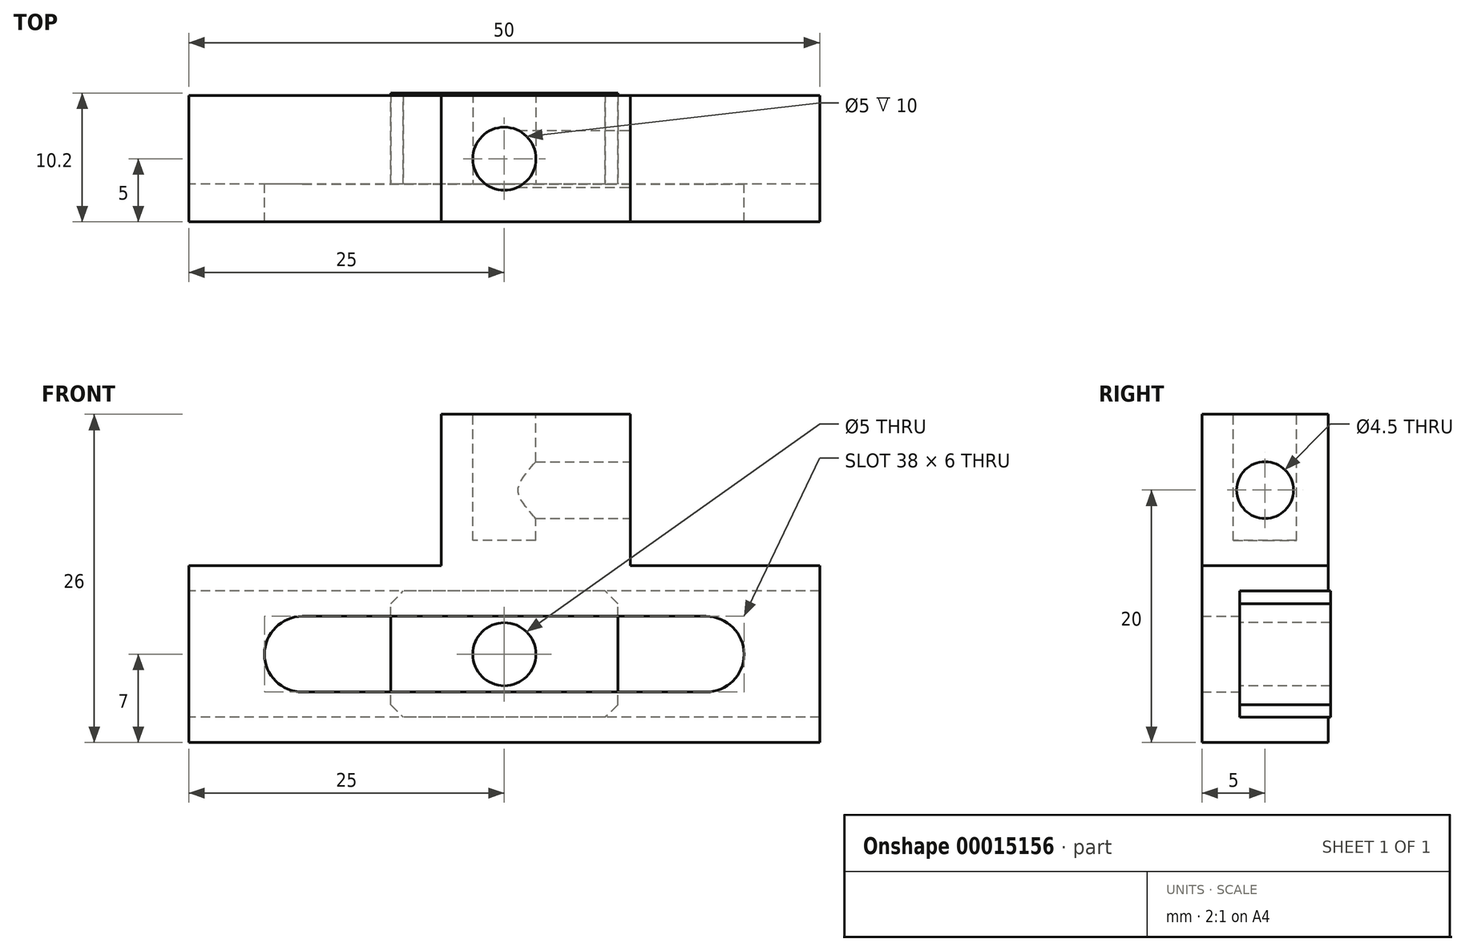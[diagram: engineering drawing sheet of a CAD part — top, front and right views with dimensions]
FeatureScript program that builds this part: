
annotation { "Feature Type Name" : "Feature", "Feature Type Description" : "" }
export const myFeature = defineFeature(function(context is Context, id is Id, definition is map)
    precondition{}
    {
        {
            var Q0;
            Q0=qCreatedBy(makeId("Right.planeOp"),FACE);
            var sketch = newSketch(context, id + "F0", { "sketchPlane" : qUnion([Q0])});
            skLineSegment(sketch, "E0.rect.bottom", {"start": v(5, -7) * mm, "end": v(-5, -7) * mm});
            skLineSegment(sketch, "E0.rect.top", {"start": v(5, 7) * mm, "end": v(-5, 7) * mm});
            skLineSegment(sketch, "E0.rect.left", {"start": v(5, -7) * mm, "end": v(5, -5) * mm});
            skLineSegment(sketch, "E0.rect.right", {"start": v(-5, -7) * mm, "end": v(-5, 7) * mm});
            skPoint(sketch, "E0.rect.middle", {"position": v(0, 0) * mm});
            skLineSegment(sketch, "E1", {"start": v(5, 5) * mm, "end": v(-2, 5) * mm});
            skLineSegment(sketch, "E2", {"start": v(-2, 5) * mm, "end": v(-2, -5) * mm});
            skLineSegment(sketch, "E3", {"start": v(-2, -5) * mm, "end": v(5, -5) * mm});
            skLineSegment(sketch, "E4", {"start": v(7.33, 0) * mm, "end": v(-10.47, 0) * mm, "construction": true});
            skLineSegment(sketch, "E5.trimOffspring", {"start": v(5, 5) * mm, "end": v(5, 7) * mm});
            skSolve(sketch);
        }
        {
            var Q0;
            Q0=makeQuery(id+"F0.imprint","IMPRINT",FACE,{"disambiguationData":[TD([[makeQuery(id+"F0.imprint","IMPRINT",EDGE,{"derivedFrom":sQuery(id+"F0.wireOp",EDGE,"E0.rect.bottom")}),-1.0]])]});
            extrude(context, id + "F1", {"entities" : qUnion([Q0]), "endBound" : BoundingType.SYMMETRIC, "depth" : 50 * mm});
        }
        {
            var Q0;
            Q0=makeQuery(id+"F1.opExtrude","SWEPT_FACE",FACE,{"disambiguationData":[OSD([sQuery(id+"F0.wireOp",EDGE,"E2")])]});
            var sketch = newSketch(context, id + "F2", { "sketchPlane" : qUnion([Q0])});
            skLineSegment(sketch, "E6", {"start": v(25, 0) * mm, "end": v(-25, 0) * mm, "construction": true});
            skPoint(sketch, "E7", {"position": v(-16, 0) * mm});
            skPoint(sketch, "E8", {"position": v(16, 0) * mm});
            skLineSegment(sketch, "E9", {"start": v(0, 0) * mm, "end": v(0, 7.81) * mm, "construction": true});
            skArc(sketch, "E10", {"start": v(-16, 3) * mm, "mid": v(-19, 0) * mm, "end": v(-16, -3) * mm});
            skArc(sketch, "E11", {"start": v(16, -3) * mm, "mid": v(19, 0) * mm, "end": v(16, 3) * mm});
            skLineSegment(sketch, "E12", {"start": v(-16, -3) * mm, "end": v(16, -3) * mm});
            skLineSegment(sketch, "E13", {"start": v(16, 3) * mm, "end": v(-16, 3) * mm});
            skSolve(sketch);
        }
        {
            var Q0;
            Q0=makeQuery(id+"F2.imprint","IMPRINT",FACE,{"disambiguationData":[TD([[makeQuery(id+"F2.imprint","IMPRINT",EDGE,{"derivedFrom":sQuery(id+"F2.wireOp",EDGE,"E10")}),1.0]])]});
            extrude(context, id + "F3", {"entities" : qUnion([Q0]), "operationType" : NewBodyOperationType.REMOVE, "endBound" : BoundingType.THROUGH_ALL, "oppositeDirection" : true, "depth" : 25 * mm});
        }
        {
            var Q0;
            Q0=makeQuery(id+"F1.opExtrude","SWEPT_FACE",FACE,{"disambiguationData":[OSD([sQuery(id+"F0.wireOp",EDGE,"E0.rect.top")])]});
            var sketch = newSketch(context, id + "F4", { "sketchPlane" : qUnion([Q0])});
            skLineSegment(sketch, "E14.bottom", {"start": v(10, -5) * mm, "end": v(-5, -5) * mm});
            skLineSegment(sketch, "E14.top", {"start": v(10, 5) * mm, "end": v(-5, 5) * mm});
            skLineSegment(sketch, "E14.left", {"start": v(10, -5) * mm, "end": v(10, 5) * mm});
            skLineSegment(sketch, "E14.right", {"start": v(-5, -5) * mm, "end": v(-5, 5) * mm});
            skSolve(sketch);
        }
        {
            var Q0;
            Q0=makeQuery(id+"F4.imprint","IMPRINT",FACE,{"disambiguationData":[TD([[makeQuery(id+"F4.imprint","IMPRINT",EDGE,{"derivedFrom":sQuery(id+"F4.wireOp",EDGE,"E14.bottom")}),-1.0]])]});
            extrude(context, id + "F5", {"entities" : qUnion([Q0]), "operationType" : NewBodyOperationType.ADD, "depth" : (26 - 14) * mm});
        }
        {
            var Q0;
            Q0=makeQuery(id+"F5.opExtrude","CAP_FACE",FACE,{"disambiguationData":[OSD([sQuery(id+"F4.wireOp",EDGE,"E14.bottom"),sQuery(id+"F4.wireOp",EDGE,"E14.top"),sQuery(id+"F4.wireOp",EDGE,"E14.left"),sQuery(id+"F4.wireOp",EDGE,"E14.right")])],"isStart":false});
            var sketch = newSketch(context, id + "F6", { "sketchPlane" : qUnion([Q0])});
            skCircle(sketch, "E15", {"center": v(0, 0) * mm, "radius": 2.5 * mm});
            skSolve(sketch);
        }
        {
            var Q0;
            Q0=makeQuery(id+"F6.imprint","IMPRINT",FACE,{"disambiguationData":[TD([[makeQuery(id+"F6.imprint","IMPRINT",EDGE,{"derivedFrom":sQuery(id+"F6.wireOp",EDGE,"E15")}),1.0]])]});
            extrude(context, id + "F7", {"entities" : qUnion([Q0]), "operationType" : NewBodyOperationType.REMOVE, "oppositeDirection" : true, "depth" : 10 * mm});
        }
        {
            var Q0;
            Q0=makeQuery(id+"F5.opExtrude","SWEPT_FACE",FACE,{"disambiguationData":[OSD([sQuery(id+"F4.wireOp",EDGE,"E14.left")])]});
            var sketch = newSketch(context, id + "F8", { "sketchPlane" : qUnion([Q0])});
            skLineSegment(sketch, "E16", {"start": v(0, 19) * mm, "end": v(0, 7) * mm, "construction": true});
            skLineSegment(sketch, "E17", {"start": v(-5, 13) * mm, "end": v(5, 13) * mm, "construction": true});
            skCircle(sketch, "E18", {"center": v(0, 13) * mm, "radius": 2.25 * mm});
            skSolve(sketch);
        }
        {
            var Q0;
            Q0=makeQuery(id+"F8.imprint","IMPRINT",FACE,{"disambiguationData":[TD([[makeQuery(id+"F8.imprint","IMPRINT",EDGE,{"derivedFrom":sQuery(id+"F8.wireOp",EDGE,"E18")}),1.0]])]});
            var Q1;
            Q1=makeQuery(id+"F7.boolean.opBoolean","COPY",FACE,{"derivedFrom":makeQuery(id+"F7.opExtrude","CAP_FACE",FACE,{"disambiguationData":[OSD([sQuery(id+"F6.wireOp",EDGE,"E15")])],"isStart":false})});
            extrude(context, id + "F9", {"entities" : qUnion([Q0]), "operationType" : NewBodyOperationType.REMOVE, "endBound" : BoundingType.UP_TO_BODY, "oppositeDirection" : true, "endBoundEntityBody" : qUnion([Q1]), "depth" : 25 * mm});
        }
        {
            var Q0;
            Q0=makeQuery(id+"F1.opExtrude","SWEPT_FACE",FACE,{"disambiguationData":[OSD([sQuery(id+"F0.wireOp",EDGE,"E2")])]});
            var sketch = newSketch(context, id + "F10", { "sketchPlane" : qUnion([Q0])});
            skLineSegment(sketch, "E19.rect.bottom", {"start": v(9, -5) * mm, "end": v(-9, -5) * mm});
            skLineSegment(sketch, "E19.rect.top", {"start": v(9, 5) * mm, "end": v(-9, 5) * mm});
            skLineSegment(sketch, "E19.rect.left", {"start": v(9, -5) * mm, "end": v(9, 5) * mm});
            skLineSegment(sketch, "E19.rect.right", {"start": v(-9, -5) * mm, "end": v(-9, 5) * mm});
            skPoint(sketch, "E19.rect.middle", {"position": v(0, 0) * mm});
            skCircle(sketch, "E20", {"center": v(0, 0) * mm, "radius": 2.5 * mm});
            skSolve(sketch);
        }
        {
            var Q0;
            Q0=makeQuery(id+"F10.imprint","IMPRINT",FACE,{"disambiguationData":[TD([[makeQuery(id+"F10.imprint","IMPRINT",EDGE,{"derivedFrom":sQuery(id+"F10.wireOp",EDGE,"E20")}),-1.0]])]});
            var Q1;
            {var subQ4=sQuery(id+"F10.wireOp",EDGE,"E19.rect.top");Q1=makeQuery(id+"F10.imprint","IMPRINT",FACE,{"disambiguationData":[TD([[makeQuery(id+"F10.imprint","IMPRINT",EDGE,{"derivedFrom":subQ4}),-1.0]])]});}
            var Q2;
            {var subQ6=sQuery(id+"F10.wireOp",EDGE,"E19.rect.bottom");Q2=makeQuery(id+"F10.imprint","IMPRINT",FACE,{"disambiguationData":[TD([[makeQuery(id+"F10.imprint","IMPRINT",EDGE,{"derivedFrom":subQ6}),1.0]])]});}
            extrude(context, id + "F11", {"entities" : qUnion([Q0, Q1, Q2]), "depth" : 7.2 * mm});
        }
        {
            var Q0;
            Q0=makeQuery(id+"F11.opExtrude","SWEPT_EDGE",EDGE,{"disambiguationData":[OSD([sQuery(id+"F0.wireOp",EDGE,"E1"),sQuery(id+"F0.wireOp",EDGE,"E2"),sQuery(id+"F10.wireOp",EDGE,"E19.rect.top"),sQuery(id+"F10.wireOp",EDGE,"E19.rect.left")])]});
            var Q1;
            Q1=makeQuery(id+"F11.opExtrude","SWEPT_EDGE",EDGE,{"disambiguationData":[OSD([sQuery(id+"F0.wireOp",EDGE,"E1"),sQuery(id+"F0.wireOp",EDGE,"E2"),sQuery(id+"F10.wireOp",EDGE,"E19.rect.top"),sQuery(id+"F10.wireOp",EDGE,"E19.rect.right")])]});
            var Q2;
            Q2=makeQuery(id+"F11.opExtrude","SWEPT_EDGE",EDGE,{"disambiguationData":[OSD([sQuery(id+"F0.wireOp",EDGE,"E2"),sQuery(id+"F0.wireOp",EDGE,"E3"),sQuery(id+"F10.wireOp",EDGE,"E19.rect.bottom"),sQuery(id+"F10.wireOp",EDGE,"E19.rect.left")])]});
            var Q3;
            Q3=makeQuery(id+"F11.opExtrude","SWEPT_EDGE",EDGE,{"disambiguationData":[OSD([sQuery(id+"F0.wireOp",EDGE,"E2"),sQuery(id+"F0.wireOp",EDGE,"E3"),sQuery(id+"F10.wireOp",EDGE,"E19.rect.bottom"),sQuery(id+"F10.wireOp",EDGE,"E19.rect.right")])]});
            chamfer(context, id + "F12", {"entities" : qUnion([Q0, Q1, Q2, Q3]), "width" : 1 * mm, "tangentPropagation" : true});
        }
    });
